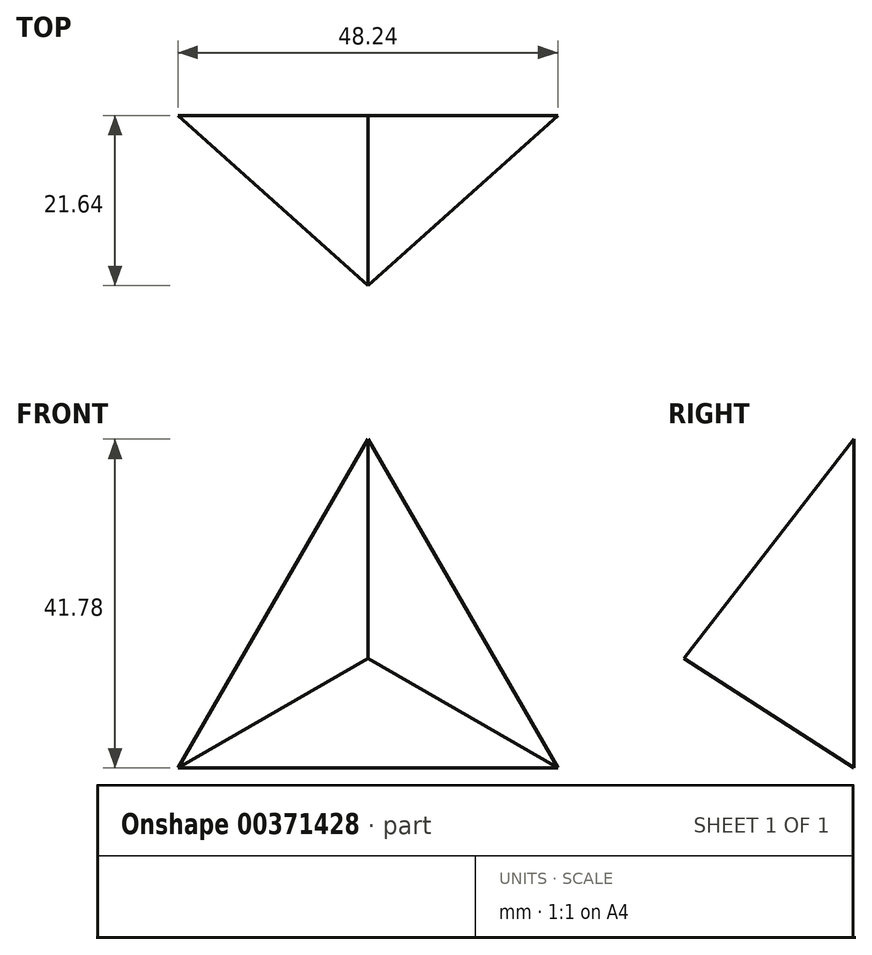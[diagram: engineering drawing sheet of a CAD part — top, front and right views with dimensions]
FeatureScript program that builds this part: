
annotation { "Feature Type Name" : "Feature", "Feature Type Description" : "" }
export const myFeature = defineFeature(function(context is Context, id is Id, definition is map)
    precondition{}
    {
        {
            var Q0;
            Q0=qCreatedBy(makeId("Front.planeOp"),FACE);
            var sketch = newSketch(context, id + "F0", { "sketchPlane" : qUnion([Q0])});
            skCircle(sketch, "E0.cCircle", {"center": v(0, 0) * mm, "radius": 13.93 * mm, "construction": true});
            skLineSegment(sketch, "E0.0", {"start": v(-24.12, -13.93) * mm, "end": v(0, 27.85) * mm});
            skLineSegment(sketch, "E0.1", {"start": v(0, 27.85) * mm, "end": v(24.12, -13.93) * mm});
            skLineSegment(sketch, "E0.2", {"start": v(24.12, -13.93) * mm, "end": v(-24.12, -13.93) * mm});
            skPoint(sketch, "E0.0.midPoint", {"position": v(-12.06, 6.96) * mm});
            skSolve(sketch);
        }
        {
            var Q0;
            Q0=makeQuery(id+"F0.imprint","IMPRINT",FACE,{"disambiguationData":[TD([[makeQuery(id+"F0.imprint","IMPRINT",EDGE,{"derivedFrom":sQuery(id+"F0.wireOp",EDGE,"E0.0")}),-1.0]])]});
            extrude(context, id + "F1", {"entities" : qUnion([Q0]), "depth" : 50.8 * mm});
        }
        {
            var Q0;
            Q0=makeQuery(id+"F1.opExtrude","CAP_VERTEX",VERTEX,{"disambiguationData":[OSD([sQuery(id+"F0.wireOp",EDGE,"E0.0"),sQuery(id+"F0.wireOp",EDGE,"E0.2")])],"isStart":false});
            var Q1;
            Q1=makeQuery(id+"F1.opExtrude","CAP_EDGE",EDGE,{"disambiguationData":[OSD([sQuery(id+"F0.wireOp",EDGE,"E0.0")])],"isStart":false});
            cPlane(context, id + "F2", {"entities" : qUnion([Q0, Q1]), "cplaneType" : CPlaneType.LINE_POINT, "offset" : 25.4 * mm, "width" : 152.4 * mm, "height" : 152.4 * mm});
        }
        {
            var Q0;
            Q0=qCreatedBy(makeId("Right.planeOp"),FACE);
            var sketch = newSketch(context, id + "F3", { "sketchPlane" : qUnion([Q0])});
            skLineSegment(sketch, "E1.0.0", {"start": v(0, 27.85) * mm, "end": v(0, -13.93) * mm, "construction": true});
            skLineSegment(sketch, "E1.0.1", {"start": v(0, -13.93) * mm, "end": v(-50.8, -13.93) * mm, "construction": true});
            skLineSegment(sketch, "E1.0.2", {"start": v(-50.8, -13.93) * mm, "end": v(-50.8, 27.85) * mm, "construction": true});
            skLineSegment(sketch, "E1.0.3", {"start": v(-50.8, 27.85) * mm, "end": v(0, 27.85) * mm, "construction": true});
            skLineSegment(sketch, "E2", {"start": v(0, -13.93) * mm, "end": v(-21.64, 0) * mm});
            skLineSegment(sketch, "E3", {"start": v(-21.64, 0) * mm, "end": v(-53.45, 0) * mm});
            skLineSegment(sketch, "E4", {"start": v(-53.45, 0) * mm, "end": v(-53.45, -20.19) * mm});
            skLineSegment(sketch, "E5", {"start": v(-53.45, -20.19) * mm, "end": v(-4.14, -23.69) * mm});
            skLineSegment(sketch, "E6", {"start": v(-4.14, -23.69) * mm, "end": v(0, -13.93) * mm});
            skSolve(sketch);
        }
        {
            var Q0;
            Q0=makeQuery(id+"F3.imprint","IMPRINT",FACE,{"disambiguationData":[TD([[makeQuery(id+"F3.imprint","IMPRINT",EDGE,{"derivedFrom":sQuery(id+"F3.wireOp",EDGE,"E2")}),1.0]])]});
            extrude(context, id + "F4", {"entities" : qUnion([Q0]), "operationType" : NewBodyOperationType.REMOVE, "endBound" : BoundingType.SYMMETRIC, "oppositeDirection" : true, "depth" : 76.2 * mm});
        }
        {
            var Q0;
            Q0=qCreatedBy(id+"F2.planeOp",FACE);
            var sketch = newSketch(context, id + "F5", { "sketchPlane" : qUnion([Q0])});
            skLineSegment(sketch, "E7.0.0", {"start": v(27.85, 0) * mm, "end": v(13.93, -21.64) * mm, "construction": true});
            skLineSegment(sketch, "E7.0.1", {"start": v(13.93, -21.64) * mm, "end": v(-13.93, -21.64) * mm, "construction": true});
            skLineSegment(sketch, "E7.0.2", {"start": v(-13.93, -21.64) * mm, "end": v(-13.93, 0) * mm, "construction": true});
            skLineSegment(sketch, "E7.0.3", {"start": v(-13.93, 0) * mm, "end": v(27.85, 0) * mm, "construction": true});
            skLineSegment(sketch, "E8", {"start": v(-13.93, 0) * mm, "end": v(0, -21.64) * mm});
            skLineSegment(sketch, "E9", {"start": v(0, -21.64) * mm, "end": v(0, -58.66) * mm});
            skLineSegment(sketch, "E10", {"start": v(0, -58.66) * mm, "end": v(-23.68, -57.1) * mm});
            skLineSegment(sketch, "E11", {"start": v(-23.68, -57.1) * mm, "end": v(-13.93, 0) * mm});
            skSolve(sketch);
        }
        {
            var Q0;
            Q0=makeQuery(id+"F5.imprint","IMPRINT",FACE,{"disambiguationData":[TD([[makeQuery(id+"F5.imprint","IMPRINT",EDGE,{"derivedFrom":sQuery(id+"F5.wireOp",EDGE,"E8")}),-1.0]])]});
            extrude(context, id + "F6", {"entities" : qUnion([Q0]), "operationType" : NewBodyOperationType.REMOVE, "depth" : 76.2 * mm});
        }
        {
            var Q0;
            {var subQ0=sQuery(id+"F0.wireOp",EDGE,"E0.1");Q0=makeQuery(id+"F6.boolean.opBoolean","INTERSECT",VERTEX,{"derivedFrom":[makeQuery(id+"F1.opExtrude","CAP_FACE",FACE,{"disambiguationData":[OSD([sQuery(id+"F0.wireOp",EDGE,"E0.0"),subQ0,sQuery(id+"F0.wireOp",EDGE,"E0.2")])],"isStart":false}),makeQuery(id+"F1.opExtrude","SWEPT_FACE",FACE,{"disambiguationData":[OSD([subQ0])]}),makeQuery(id+"F6.opExtrude","SWEPT_FACE",FACE,{"disambiguationData":[OSD([sQuery(id+"F5.wireOp",EDGE,"E9")])]})]});}
            var Q1;
            Q1=makeQuery(id+"F1.opExtrude","CAP_EDGE",EDGE,{"disambiguationData":[OSD([sQuery(id+"F0.wireOp",EDGE,"E0.1")])],"isStart":false});
            cPlane(context, id + "F7", {"entities" : qUnion([Q0, Q1]), "cplaneType" : CPlaneType.LINE_POINT, "offset" : 25.4 * mm, "width" : 152.4 * mm, "height" : 152.4 * mm});
        }
        {
            var Q0;
            Q0=qCreatedBy(id+"F7.planeOp",FACE);
            var sketch = newSketch(context, id + "F8", { "sketchPlane" : qUnion([Q0])});
            skLineSegment(sketch, "E12.0.0", {"start": v(13.93, 21.64) * mm, "end": v(13.93, 0) * mm, "construction": true});
            skLineSegment(sketch, "E12.0.1", {"start": v(13.93, 0) * mm, "end": v(-27.85, 0) * mm, "construction": true});
            skLineSegment(sketch, "E12.0.2", {"start": v(-27.85, 0) * mm, "end": v(0, 21.64) * mm, "construction": true});
            skLineSegment(sketch, "E12.0.3", {"start": v(0, 21.64) * mm, "end": v(13.93, 21.64) * mm, "construction": true});
            skLineSegment(sketch, "E13", {"start": v(0, 21.64) * mm, "end": v(13.93, 0) * mm});
            skLineSegment(sketch, "E14", {"start": v(13.93, 0) * mm, "end": v(24.4, 42.08) * mm});
            skLineSegment(sketch, "E15", {"start": v(24.4, 42.08) * mm, "end": v(17.78, 52.33) * mm});
            skLineSegment(sketch, "E16", {"start": v(17.78, 52.33) * mm, "end": v(-6.02, 52.33) * mm});
            skLineSegment(sketch, "E17", {"start": v(-6.02, 52.33) * mm, "end": v(0, 21.64) * mm});
            skSolve(sketch);
        }
        {
            var Q0;
            Q0=makeQuery(id+"F8.imprint","IMPRINT",FACE,{"disambiguationData":[TD([[makeQuery(id+"F8.imprint","IMPRINT",EDGE,{"derivedFrom":sQuery(id+"F8.wireOp",EDGE,"E13")}),1.0]])]});
            extrude(context, id + "F9", {"entities" : qUnion([Q0]), "operationType" : NewBodyOperationType.REMOVE, "endBound" : BoundingType.SYMMETRIC, "oppositeDirection" : true, "depth" : 76.2 * mm});
        }
    });
